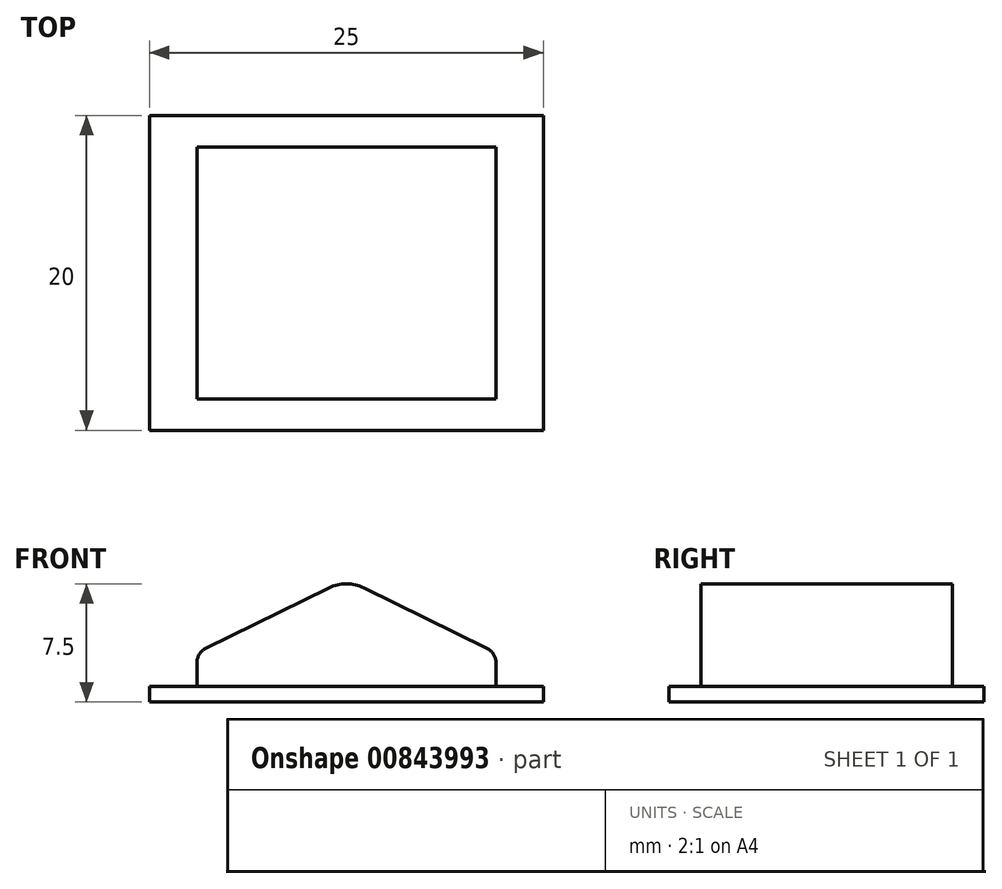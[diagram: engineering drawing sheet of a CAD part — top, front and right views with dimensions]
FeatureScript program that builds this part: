
annotation { "Feature Type Name" : "Feature", "Feature Type Description" : "" }
export const myFeature = defineFeature(function(context is Context, id is Id, definition is map)
    precondition{}
    {
        {
            var Q0;
            Q0=qCreatedBy(makeId("Top.planeOp"),FACE);
            var sketch = newSketch(context, id + "F0", { "sketchPlane" : qUnion([Q0])});
            skLineSegment(sketch, "E0.bottom", {"start": v(-12.5, 10) * mm, "end": v(12.5, 10) * mm});
            skLineSegment(sketch, "E0.top", {"start": v(-12.5, -10) * mm, "end": v(12.5, -10) * mm});
            skLineSegment(sketch, "E0.left", {"start": v(-12.5, 10) * mm, "end": v(-12.5, -10) * mm});
            skLineSegment(sketch, "E0.right", {"start": v(12.5, 10) * mm, "end": v(12.5, -10) * mm});
            skPoint(sketch, "E0.middle", {"position": v(0, 0) * mm});
            skSolve(sketch);
        }
        {
            var Q0;
            Q0=makeQuery(id+"F0.imprint","IMPRINT",FACE,{"disambiguationData":[TD([[makeQuery(id+"F0.imprint","IMPRINT",EDGE,{"derivedFrom":sQuery(id+"F0.wireOp",EDGE,"E0.bottom")}),-1.0]])]});
            extrude(context, id + "F1", {"entities" : qUnion([Q0]), "depth" : 1 * mm, "offsetDistance" : 25 * mm});
        }
        {
            var Q0;
            Q0=qCreatedBy(makeId("Front.planeOp"),FACE);
            var sketch = newSketch(context, id + "F2", { "sketchPlane" : qUnion([Q0])});
            skArc(sketch, "E1", {"start": v(1.1, 7.24) * mm, "mid": v(0, 7.5) * mm, "end": v(-1.1, 7.24) * mm});
            skArc(sketch, "E2", {"start": v(9.5, 2.5) * mm, "mid": v(9.35, 3.03) * mm, "end": v(8.94, 3.4) * mm});
            skArc(sketch, "E3", {"start": v(-8.94, 3.4) * mm, "mid": v(-9.35, 3.03) * mm, "end": v(-9.5, 2.5) * mm});
            skLineSegment(sketch, "E4", {"start": v(1.1, 7.24) * mm, "end": v(8.94, 3.4) * mm});
            skLineSegment(sketch, "E5", {"start": v(9.5, 2.5) * mm, "end": v(9.5, 1) * mm});
            skLineSegment(sketch, "E6", {"start": v(-9.5, 1) * mm, "end": v(9.5, 1) * mm});
            skLineSegment(sketch, "E7", {"start": v(-1.1, 7.24) * mm, "end": v(-8.94, 3.4) * mm});
            skLineSegment(sketch, "E8", {"start": v(-9.5, 1) * mm, "end": v(-9.5, 2.5) * mm});
            skSolve(sketch);
        }
        {
            var Q0;
            Q0=makeQuery(id+"F2.imprint","IMPRINT",FACE,{"disambiguationData":[TD([[makeQuery(id+"F2.imprint","IMPRINT",EDGE,{"derivedFrom":sQuery(id+"F2.wireOp",EDGE,"E1")}),1.0]])]});
            extrude(context, id + "F3", {"entities" : qUnion([Q0]), "operationType" : NewBodyOperationType.ADD, "endBound" : BoundingType.SYMMETRIC, "depth" : 16 * mm, "offsetDistance" : 25 * mm});
        }
    });
